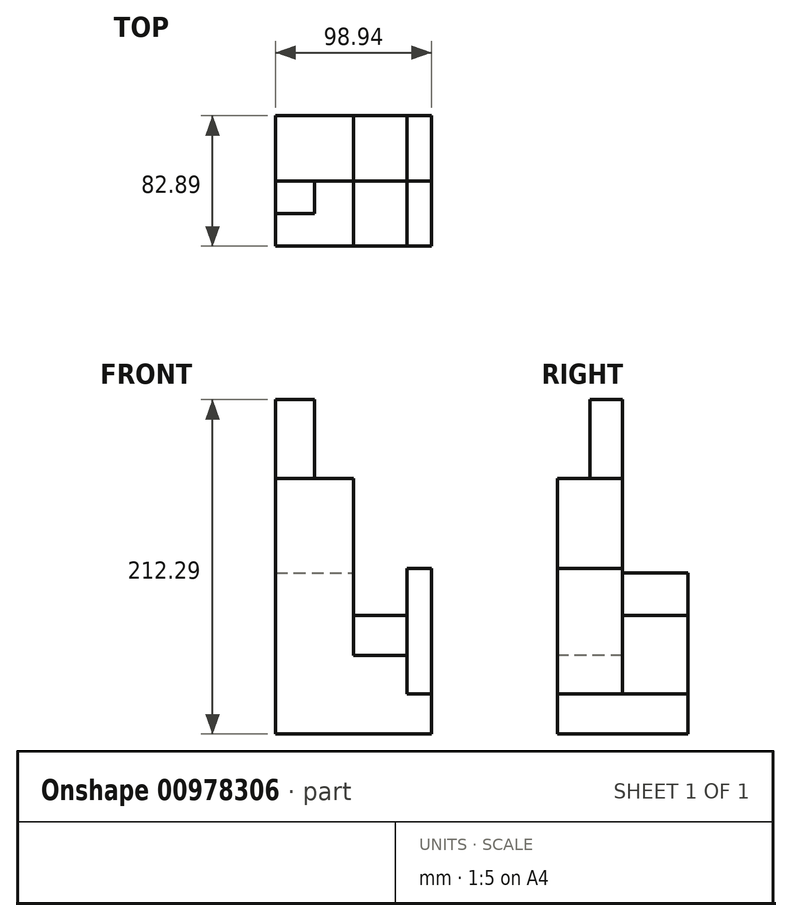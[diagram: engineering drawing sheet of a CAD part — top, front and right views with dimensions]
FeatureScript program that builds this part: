
annotation { "Feature Type Name" : "Feature", "Feature Type Description" : "" }
export const myFeature = defineFeature(function(context is Context, id is Id, definition is map)
    precondition{}
    {
        {
            var Q0;
            Q0=qCreatedBy(makeId("Top.planeOp"),FACE);
            var sketch = newSketch(context, id + "F0", { "sketchPlane" : qUnion([Q0])});
            skLineSegment(sketch, "E0.bottom", {"start": v(-39.24, 37.12) * mm, "end": v(59.7, 37.12) * mm});
            skLineSegment(sketch, "E0.top", {"start": v(-39.24, -45.77) * mm, "end": v(59.7, -45.77) * mm});
            skLineSegment(sketch, "E0.left", {"start": v(-39.24, 37.12) * mm, "end": v(-39.24, -45.77) * mm});
            skLineSegment(sketch, "E0.right", {"start": v(59.7, 37.12) * mm, "end": v(59.7, -45.77) * mm});
            skLineSegment(sketch, "E1.bottom", {"start": v(10.23, 37.12) * mm, "end": v(44.18, 37.12) * mm});
            skLineSegment(sketch, "E1.top", {"start": v(10.23, -45.77) * mm, "end": v(44.18, -45.77) * mm});
            skLineSegment(sketch, "E1.left", {"start": v(10.23, 37.12) * mm, "end": v(10.23, -45.77) * mm});
            skLineSegment(sketch, "E1.right", {"start": v(44.18, 37.12) * mm, "end": v(44.18, -45.77) * mm});
            skSolve(sketch);
        }
        {
            var Q0;
            {var subQ0=sQuery(id+"F0.wireOp",EDGE,"E0.left");Q0=makeQuery(id+"F0.imprint","IMPRINT",FACE,{"disambiguationData":[TD([[makeQuery(id+"F0.imprint","IMPRINT",EDGE,{"derivedFrom":subQ0}),1.0]])]});}
            extrude(context, id + "F1", {"entities" : qUnion([Q0]), "depth" : 102.34 * mm, "offsetDistance" : 25.4 * mm});
        }
        {
            var Q0;
            {var subQ0=sQuery(id+"F0.wireOp",EDGE,"E1.left");Q0=makeQuery(id+"F0.imprint","IMPRINT",FACE,{"disambiguationData":[TD([[makeQuery(id+"F0.imprint","IMPRINT",EDGE,{"derivedFrom":subQ0}),1.0]])]});}
            extrude(context, id + "F2", {"entities" : qUnion([Q0]), "operationType" : NewBodyOperationType.ADD, "depth" : 49.83 * mm, "offsetDistance" : 25.4 * mm});
        }
        {
            var Q0;
            {var subQ0=sQuery(id+"F0.wireOp",EDGE,"E0.right");Q0=makeQuery(id+"F0.imprint","IMPRINT",FACE,{"disambiguationData":[TD([[makeQuery(id+"F0.imprint","IMPRINT",EDGE,{"derivedFrom":subQ0}),-1.0]])]});}
            extrude(context, id + "F3", {"entities" : qUnion([Q0]), "operationType" : NewBodyOperationType.ADD, "depth" : 25.4 * mm, "offsetDistance" : 25.4 * mm});
        }
        {
            var Q0;
            Q0=makeQuery(id+"F1.opExtrude","CAP_FACE",FACE,{"disambiguationData":[OSD([sQuery(id+"F0.wireOp",EDGE,"E0.bottom"),sQuery(id+"F0.wireOp",EDGE,"E0.top"),sQuery(id+"F0.wireOp",EDGE,"E0.left"),sQuery(id+"F0.wireOp",EDGE,"E1.left")])],"isStart":false});
            var sketch = newSketch(context, id + "F4", { "sketchPlane" : qUnion([Q0])});
            skLineSegment(sketch, "E2", {"start": v(-39.24, -4.33) * mm, "end": v(10.23, -4.33) * mm});
            skSolve(sketch);
        }
        {
            var Q0;
            Q0=makeQuery(id+"F2.opExtrude","CAP_FACE",FACE,{"disambiguationData":[OSD([sQuery(id+"F0.wireOp",EDGE,"E0.bottom"),sQuery(id+"F0.wireOp",EDGE,"E0.top"),sQuery(id+"F0.wireOp",EDGE,"E1.left"),sQuery(id+"F0.wireOp",EDGE,"E1.right")])],"isStart":false});
            var sketch = newSketch(context, id + "F5", { "sketchPlane" : qUnion([Q0])});
            skLineSegment(sketch, "E3", {"start": v(44.18, -4.33) * mm, "end": v(10.23, -4.33) * mm});
            skSolve(sketch);
        }
        {
            var Q0;
            Q0=makeQuery(id+"F3.opExtrude","CAP_FACE",FACE,{"disambiguationData":[OSD([sQuery(id+"F0.wireOp",EDGE,"E0.bottom"),sQuery(id+"F0.wireOp",EDGE,"E0.top"),sQuery(id+"F0.wireOp",EDGE,"E0.right"),sQuery(id+"F0.wireOp",EDGE,"E1.right")])],"isStart":false});
            var sketch = newSketch(context, id + "F6", { "sketchPlane" : qUnion([Q0])});
            skLineSegment(sketch, "E4", {"start": v(59.7, -4.33) * mm, "end": v(44.18, -4.33) * mm});
            skSolve(sketch);
        }
        {
            var Q0;
            {var subQ0=sQuery(id+"F4.wireOp",EDGE,"E2");Q0=makeQuery(id+"F4.imprint","IMPRINT",FACE,{"disambiguationData":[TD([[makeQuery(id+"F4.imprint","IMPRINT",EDGE,{"derivedFrom":subQ0}),-1.0]])]});}
            extrude(context, id + "F7", {"entities" : qUnion([Q0]), "operationType" : NewBodyOperationType.ADD, "depth" : 59.9 * mm, "offsetDistance" : 25.4 * mm});
        }
        {
            var Q0;
            Q0=makeQuery(id+"F7.opExtrude","CAP_FACE",FACE,{"disambiguationData":[OSD([sQuery(id+"F0.wireOp",EDGE,"E0.top"),sQuery(id+"F0.wireOp",EDGE,"E0.left"),sQuery(id+"F0.wireOp",EDGE,"E1.left"),sQuery(id+"F4.wireOp",EDGE,"E2")])],"isStart":false});
            var sketch = newSketch(context, id + "F8", { "sketchPlane" : qUnion([Q0])});
            skLineSegment(sketch, "E5", {"start": v(-39.24, -25.05) * mm, "end": v(10.23, -25.05) * mm});
            skLineSegment(sketch, "E6", {"start": v(-14.5, -45.77) * mm, "end": v(-14.5, -25.05) * mm});
            skLineSegment(sketch, "E7", {"start": v(-14.5, -25.05) * mm, "end": v(-14.5, -4.33) * mm});
            skSolve(sketch);
        }
        {
            var Q0;
            {var subQ3=sQuery(id+"F8.wireOp",EDGE,"E7");Q0=makeQuery(id+"F8.imprint","IMPRINT",FACE,{"disambiguationData":[TD([[makeQuery(id+"F8.imprint","IMPRINT",EDGE,{"derivedFrom":subQ3}),1.0]])]});}
            extrude(context, id + "F9", {"entities" : qUnion([Q0]), "operationType" : NewBodyOperationType.ADD, "depth" : 50.03 * mm, "offsetDistance" : 25.4 * mm});
        }
        {
            var Q0;
            {var subQ0=sQuery(id+"F5.wireOp",EDGE,"E3");Q0=makeQuery(id+"F5.imprint","IMPRINT",FACE,{"disambiguationData":[TD([[makeQuery(id+"F5.imprint","IMPRINT",EDGE,{"derivedFrom":subQ0}),-1.0]])]});}
            extrude(context, id + "F10", {"entities" : qUnion([Q0]), "operationType" : NewBodyOperationType.ADD, "depth" : 25.4 * mm, "offsetDistance" : 25.4 * mm});
        }
        {
            var Q0;
            {var subQ0=sQuery(id+"F6.wireOp",EDGE,"E4");Q0=makeQuery(id+"F6.imprint","IMPRINT",FACE,{"disambiguationData":[TD([[makeQuery(id+"F6.imprint","IMPRINT",EDGE,{"derivedFrom":subQ0}),1.0]])]});}
            extrude(context, id + "F11", {"entities" : qUnion([Q0]), "depth" : 79.58 * mm, "offsetDistance" : 25.4 * mm});
        }
    });
